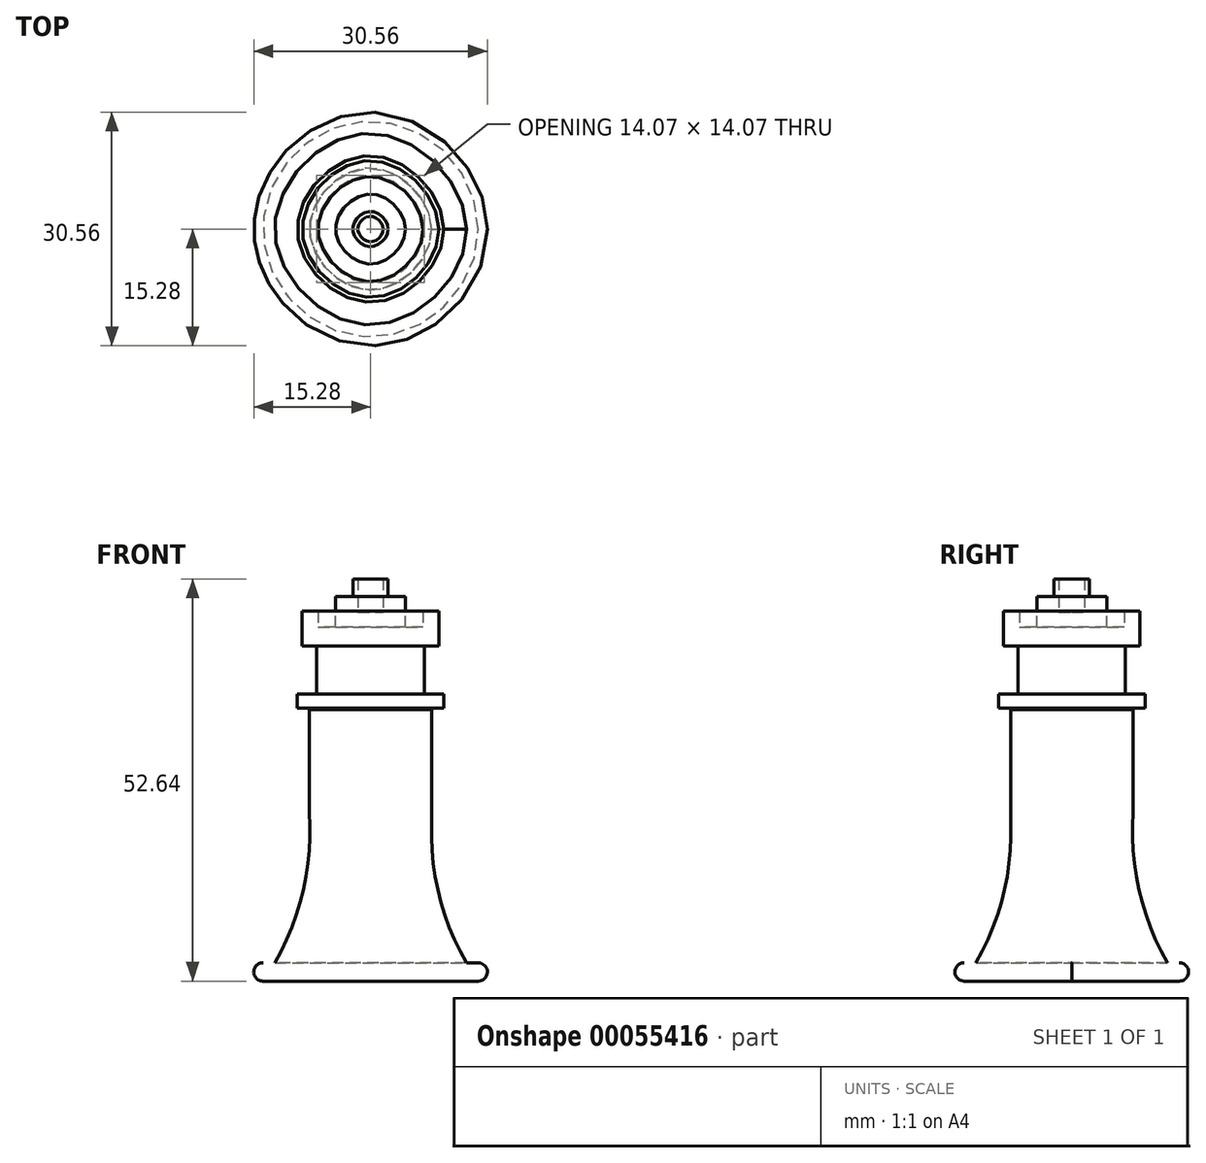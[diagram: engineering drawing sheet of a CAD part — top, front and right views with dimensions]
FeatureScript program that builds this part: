
annotation { "Feature Type Name" : "Feature", "Feature Type Description" : "" }
export const myFeature = defineFeature(function(context is Context, id is Id, definition is map)
    precondition{}
    {
        {
            var Q0;
            Q0=qCreatedBy(makeId("Top.planeOp"),FACE);
            var sketch = newSketch(context, id + "F0", { "sketchPlane" : qUnion([Q0])});
            skCircle(sketch, "E0", {"center": v(0, 0) * mm, "radius": 12.5 * mm});
            skSolve(sketch);
        }
        {
            var Q0;
            Q0=qCreatedBy(makeId("Front.planeOp"),FACE);
            var sketch = newSketch(context, id + "F1", { "sketchPlane" : qUnion([Q0])});
            skLineSegment(sketch, "E1", {"start": v(0, 0) * mm, "end": v(14.08, 0) * mm});
            skLineSegment(sketch, "E2", {"start": v(0, 0) * mm, "end": v(0, 21.06) * mm});
            skArc(sketch, "E3", {"start": v(8, 21.06) * mm, "mid": v(8.92, 11.4) * mm, "end": v(12.55, 2.4) * mm});
            skLineSegment(sketch, "E4", {"start": v(0, 21.06) * mm, "end": v(0, 48.33) * mm});
            skLineSegment(sketch, "E5", {"start": v(1.66, 52.64) * mm, "end": v(2.3, 52.64) * mm});
            skLineSegment(sketch, "E6", {"start": v(2.3, 52.64) * mm, "end": v(2.3, 50.34) * mm});
            skLineSegment(sketch, "E7", {"start": v(2.3, 50.34) * mm, "end": v(4.57, 50.34) * mm});
            skLineSegment(sketch, "E8", {"start": v(4.57, 50.34) * mm, "end": v(4.57, 46.3) * mm});
            skLineSegment(sketch, "E9", {"start": v(4.57, 46.3) * mm, "end": v(6.86, 46.3) * mm});
            skLineSegment(sketch, "E10", {"start": v(6.86, 46.3) * mm, "end": v(6.86, 48.4) * mm});
            skLineSegment(sketch, "E11", {"start": v(6.86, 48.4) * mm, "end": v(8.94, 48.4) * mm});
            skLineSegment(sketch, "E12", {"start": v(8.94, 48.4) * mm, "end": v(8.94, 43.85) * mm});
            skLineSegment(sketch, "E13", {"start": v(8.94, 43.85) * mm, "end": v(7.03, 43.85) * mm});
            skLineSegment(sketch, "E14", {"start": v(7.03, 43.85) * mm, "end": v(7.03, 37.57) * mm});
            skLineSegment(sketch, "E15", {"start": v(7.03, 37.57) * mm, "end": v(9.58, 37.57) * mm});
            skLineSegment(sketch, "E16", {"start": v(9.58, 37.57) * mm, "end": v(9.58, 35.7) * mm});
            skLineSegment(sketch, "E17", {"start": v(8, 21.06) * mm, "end": v(8, 35.54) * mm});
            skLineSegment(sketch, "E18", {"start": v(9.58, 35.7) * mm, "end": v(7.98, 35.7) * mm});
            skLineSegment(sketch, "E19", {"start": v(8, 35.54) * mm, "end": v(7.98, 35.7) * mm});
            skLineSegment(sketch, "E20", {"start": v(1.66, 52.64) * mm, "end": v(1.66, 48.33) * mm});
            skLineSegment(sketch, "E21", {"start": v(1.66, 48.33) * mm, "end": v(0, 48.33) * mm});
            skLineSegment(sketch, "E22", {"start": v(14.08, 2.4) * mm, "end": v(12.55, 2.4) * mm});
            skArc(sketch, "E23", {"start": v(14.08, 0) * mm, "mid": v(15.28, 1.2) * mm, "end": v(14.08, 2.4) * mm});
            skSolve(sketch);
        }
        {
            var Q0;
            Q0=makeQuery(id+"F1.imprint","IMPRINT",FACE,{"disambiguationData":[TD([[makeQuery(id+"F1.imprint","IMPRINT",EDGE,{"derivedFrom":sQuery(id+"F1.wireOp",EDGE,"E1")}),1.0]])]});
            var Q1;
            Q1=sQuery(id+"F0.wireOp",EDGE,"E0");
            loft(context, id + "F2", {"addGuides" : true, "sheetProfilesArray" : [{ "sheetProfileEntities" : qUnion([Q0]) }], "guidesArray" : [{ "guideEntities" : qUnion([Q1]), "guideDerivativeType" : LoftGuideDerivativeType.DEFAULT, "guideDerivativeMagnitude" : 1 }]});
        }
    });
